# Revit family: Inca Pro Baño-Ducha Empotrable
name_source: partatom
category: Plumbing Fixtures
revit_build: Autodesk Revit 2017 (Build: 20160225_1515(x64)
units: mm (PartAtom-declared; Revit-internal decimal feet)

## family parameters
Always vertical = Yes
Cut with Voids When Loaded = No
Host = Wall
OmniClass Number = 23.45.00.00
OmniClass Title = Sanitary, Laundry, and Cleaning Equipment
Part Type = Normal
Room Calculation Point = No
Round Connector Dimension = Use Diameter
Shared = No

## types (1)
- Inca Pro Baño Ducha
    Acabado Grifo = Teka_Niquel Cromo
    Acabado Logo = Teka_Pintura Logo
    CW Connection = Yes
    Ca_1_Aireador anticalcáreo cromado = Yes
    Ca_1_Brazo ducha telescópico regulable en altura = Yes
    Ca_1_Cartucho de disco cerámico = 35mm
    Ca_1_Cartucho de disco cerámico de elevada resistencia = Yes
    Ca_1_Equipo de ducha modelo = DUCAL (1 Función)
    Ca_1_Incluye flexible de ducha y soporte para equipo = Yes
    Ca_1_Modelo para Baño-Ducha = Yes
    Ca_1_Modelo para Lavamanos = No
    Ca_1_Modelo para ducha = No
    Ca_1_Modelo para ducha empotrada = No
    Ca_1_Modelo para lavamanos tipo vanitorio = No
    Ca_1_Superficie cromada de aprox. = 12,5 micras Niquel-Cromo
    Ca_Alto = 128 mm  [stored 0.419948 ft]
    Ca_Ancho = 150 mm  [stored 0.492126 ft]
    Ca_Certificaciones = Norma UNE
    Ca_Creado por = Catálogo Arquitectura
    Ca_Código Catálogo Arquitectura = 412_Tek_076
    Ca_Código EAN = 8413509205531
    Ca_Código del Producto = 552310200
    Ca_Especificaciones Técnicas = Monomando sobre muro para ducha modelo Spirit Ducha
    Ca_Fabricante = Teka
    Ca_Instalación = Sobre muro
    Ca_Itemizado CDT = E 04 00 00
    Ca_Masterformat = 22 41 39
    Ca_Material Principal = Latón con acabado en Niquel Cromo
    Ca_Medidas de embalaje = 212 x 85 x 120
    Ca_País de Fabricación = China (Planta TEKA)
    Ca_Peso = 1,75 kg
    Ca_Producto = Spirit Ducha
    Ca_Profundidad = 137 mm
    Ca_Representante = Teka
    Ca_Teléfono = 99821 1017
    Ca_Usos = Monomando para ducha
    Ca_Web del Fabricante = www.teka.cl
    Ca_Web del Representante = www.teka.cl
    Description = Monomando para ducha
    HW Connection = Yes
    Manufacturer = Teka
    Model = Spirit Ducha
    URL = www.teka.cl

note: [stored X ft] marks values corroborated as IEEE doubles in the binary element streams (Revit-internal decimal feet)

## geometry (parser evidence)
native form markers: Sweep x1
no freeform markers — native parametric forms only
